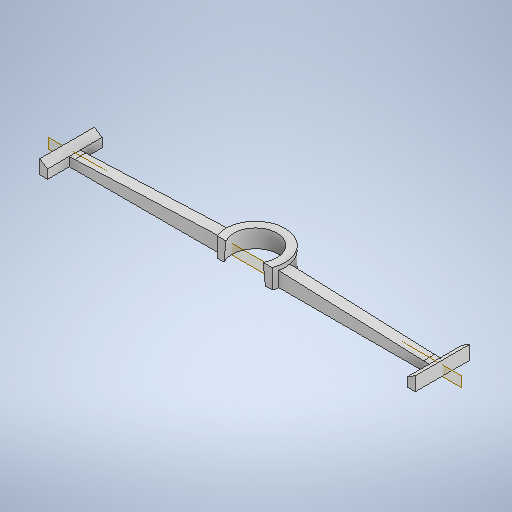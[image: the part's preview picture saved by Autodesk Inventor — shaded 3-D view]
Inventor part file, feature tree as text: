
AUTODESK INVENTOR PART (.ipt)
format: ipt  version: 2025.1 (Build 291241000, 241)  size: 356,352 bytes
history: native  units: mm
features: extrude x6, sketch x6, plane x1, other x1
ambient origin geometry x8: Origin, YZ Plane, XZ Plane, XY Plane, X Axis, Y Axis, Z Axis, Center Point
bodies: Volumenkörper1 (feature_tree)
feature tree (14):
  extrude  "Extrusion1"  Depth=4.0mm
  plane  "Arbeitsebene1"
  extrude  "Extrusion2"  Depth=2.85mm
  extrude  "Extrusion3"  Depth=19.9mm
  extrude  "Extrusion4"  Depth=7.0mm TaperAngle=0.0deg
  extrude  "Extrusion5"  Depth=53.0mm
  extrude  "Extrusion6"  Depth=55.0mm
  other  "Flächenverjüngung2"
  sketch  "Skizze1"  dims[d0=135.6mm d1=4.0mm d2=3.25mm d3=0.0mm d4=2.85mm]
  sketch  "Skizze2"  dims[d5=1.75mm d6=2.85mm]
  sketch  "Skizze3"  dims[d7=19.7mm d8=0.0mm d9=19.9mm]
  sketch  "Skizze4"  dims[d10=0.0mm d11=0.0mm d15=7.0mm d16=0.0mm]
  sketch  "Skizze5"  dims[d17=53.0mm d18=53.0mm]
  sketch  "Skizze6"  dims[d19=2.25mm d20=0.0mm d21=55.0mm d22=2.25mm d23=55.0mm d24=0.0mm d25=0.0mm d26=2.25mm d27=2.8mm d28=15.8mm d29=3.9mm d31=0.994838mm]
